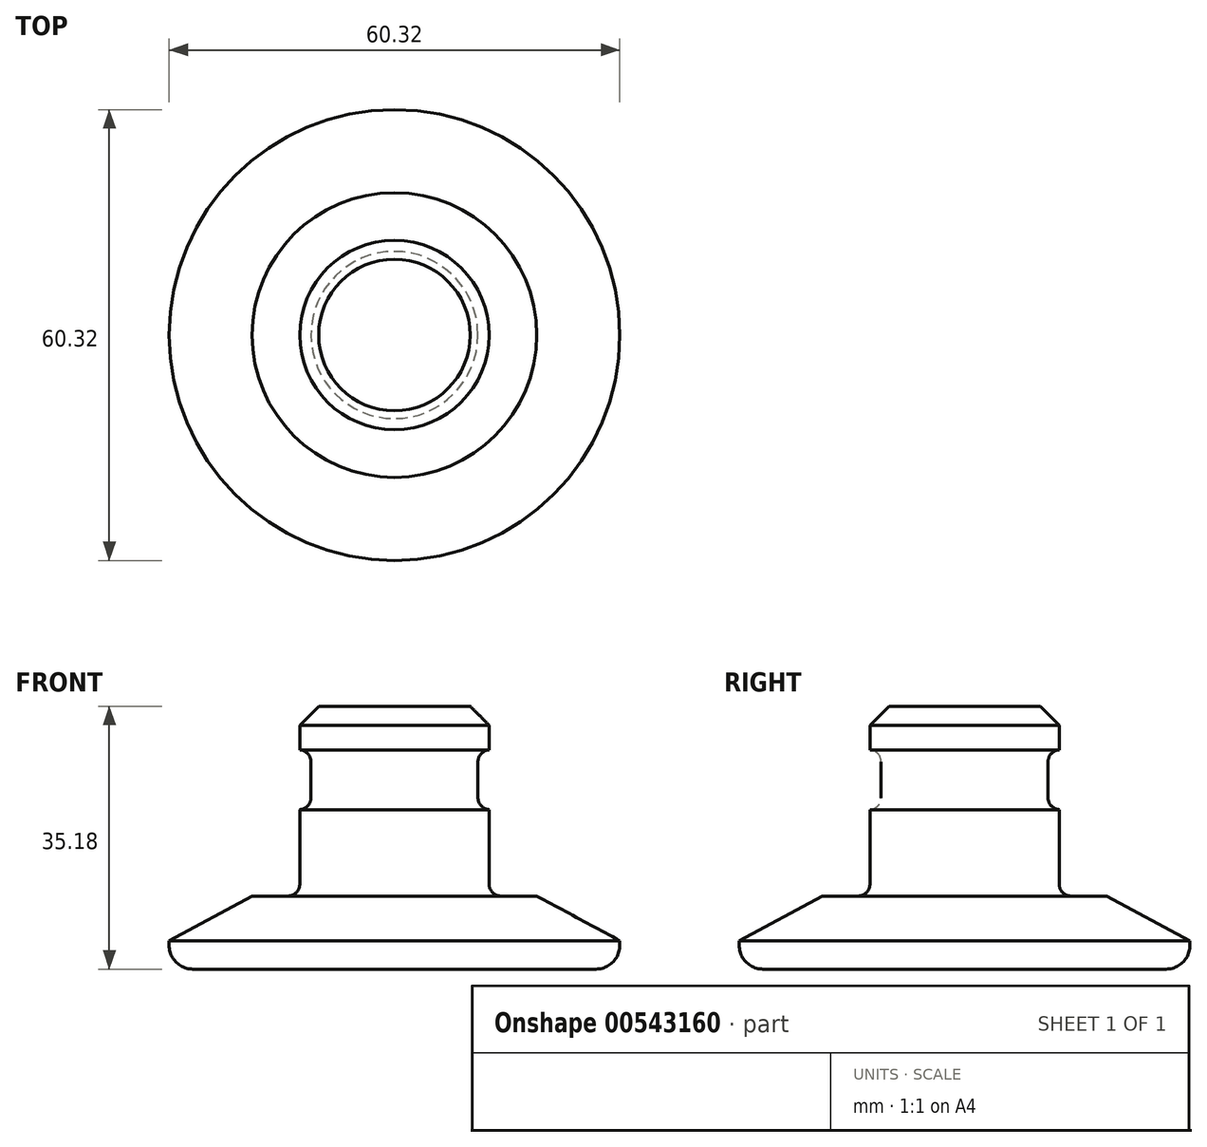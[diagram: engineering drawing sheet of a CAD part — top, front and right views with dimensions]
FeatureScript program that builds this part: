
annotation { "Feature Type Name" : "Feature", "Feature Type Description" : "" }
export const myFeature = defineFeature(function(context is Context, id is Id, definition is map)
    precondition{}
    {
        {
            var Q0;
            Q0=qCreatedBy(makeId("Front.planeOp"),FACE);
            var sketch = newSketch(context, id + "F0", { "sketchPlane" : qUnion([Q0])});
            skLineSegment(sketch, "E0", {"start": v(0, 29.67) * mm, "end": v(0, -25.5) * mm, "construction": true});
            skLineSegment(sketch, "E1", {"start": v(0, 20.48) * mm, "end": v(12.67, 20.48) * mm});
            skLineSegment(sketch, "E2", {"start": v(12.67, 20.48) * mm, "end": v(12.67, 14.64) * mm});
            skLineSegment(sketch, "E3", {"start": v(14.26, -4.92) * mm, "end": v(19.05, -4.92) * mm});
            skLineSegment(sketch, "E4", {"start": v(30.16, -10.89) * mm, "end": v(30.16, -14.7) * mm});
            skLineSegment(sketch, "E5", {"start": v(30.16, -14.7) * mm, "end": v(0, -14.7) * mm});
            skLineSegment(sketch, "E6", {"start": v(12.76, 14.64) * mm, "end": v(12.67, 14.64) * mm});
            skLineSegment(sketch, "E7", {"start": v(11.18, 13.05) * mm, "end": v(11.18, 8.22) * mm});
            skLineSegment(sketch, "E8", {"start": v(12.67, 6.64) * mm, "end": v(12.76, 6.64) * mm});
            skPoint(sketch, "E9.visualSharp", {"position": v(11.18, 14.64) * mm});
            skArc(sketch, "E9.filletArc", {"start": v(12.76, 14.64) * mm, "mid": v(11.64, 14.17) * mm, "end": v(11.18, 13.05) * mm});
            skPoint(sketch, "E10.visualSharp", {"position": v(11.18, 6.64) * mm});
            skArc(sketch, "E10.filletArc", {"start": v(11.18, 8.22) * mm, "mid": v(11.64, 7.1) * mm, "end": v(12.76, 6.64) * mm});
            skPoint(sketch, "E11.visualSharp", {"position": v(12.67, -4.92) * mm});
            skArc(sketch, "E11.filletArc", {"start": v(12.67, -3.33) * mm, "mid": v(13.14, -4.46) * mm, "end": v(14.26, -4.92) * mm});
            skLineSegment(sketch, "E12.trimOffspring", {"start": v(12.67, 6.64) * mm, "end": v(12.67, -3.33) * mm});
            skLineSegment(sketch, "E13", {"start": v(0, 20.48) * mm, "end": v(0, -14.7) * mm});
            skPoint(sketch, "E14", {"position": v(30.16, -10.89) * mm});
            skPoint(sketch, "E15", {"position": v(19.05, -4.92) * mm});
            skLineSegment(sketch, "E16", {"start": v(19.05, -4.92) * mm, "end": v(30.16, -10.89) * mm});
            skSolve(sketch);
        }
        {
            var Q0;
            {var subQ7=sQuery(id+"F0.wireOp",EDGE,"E1");Q0=makeQuery(id+"F0.imprint","IMPRINT",FACE,{"disambiguationData":[TD([[makeQuery(id+"F0.imprint","IMPRINT",EDGE,{"derivedFrom":subQ7}),-1.0]])]});}
            var Q1;
            Q1=sQuery(id+"F0.wireOp",EDGE,"E0");
            revolve(context, id + "F1", {"entities" : qUnion([Q0]), "axis" : qUnion([Q1]), "revolveType" : RevolveType.FULL});
        }
        {
            var Q0;
            Q0=makeQuery(id+"F1.opRevolve","SWEPT_EDGE",EDGE,{"disambiguationData":[OSD([sQuery(id+"F0.wireOp",EDGE,"E1"),sQuery(id+"F0.wireOp",EDGE,"E2")])]});
            chamfer(context, id + "F2", {"entities" : qUnion([Q0]), "width" : 2.54 * mm, "tangentPropagation" : true});
        }
        {
            var Q0;
            Q0=makeQuery(id+"F1.opRevolve","SWEPT_EDGE",EDGE,{"disambiguationData":[OSD([sQuery(id+"F0.wireOp",EDGE,"E4"),sQuery(id+"F0.wireOp",EDGE,"E5")])]});
            fillet(context, id + "F3", {"entities" : qUnion([Q0]), "radius" : 3.17 * mm, "tangentPropagation" : true, "allowEdgeOverflow" : false});
        }
    });
